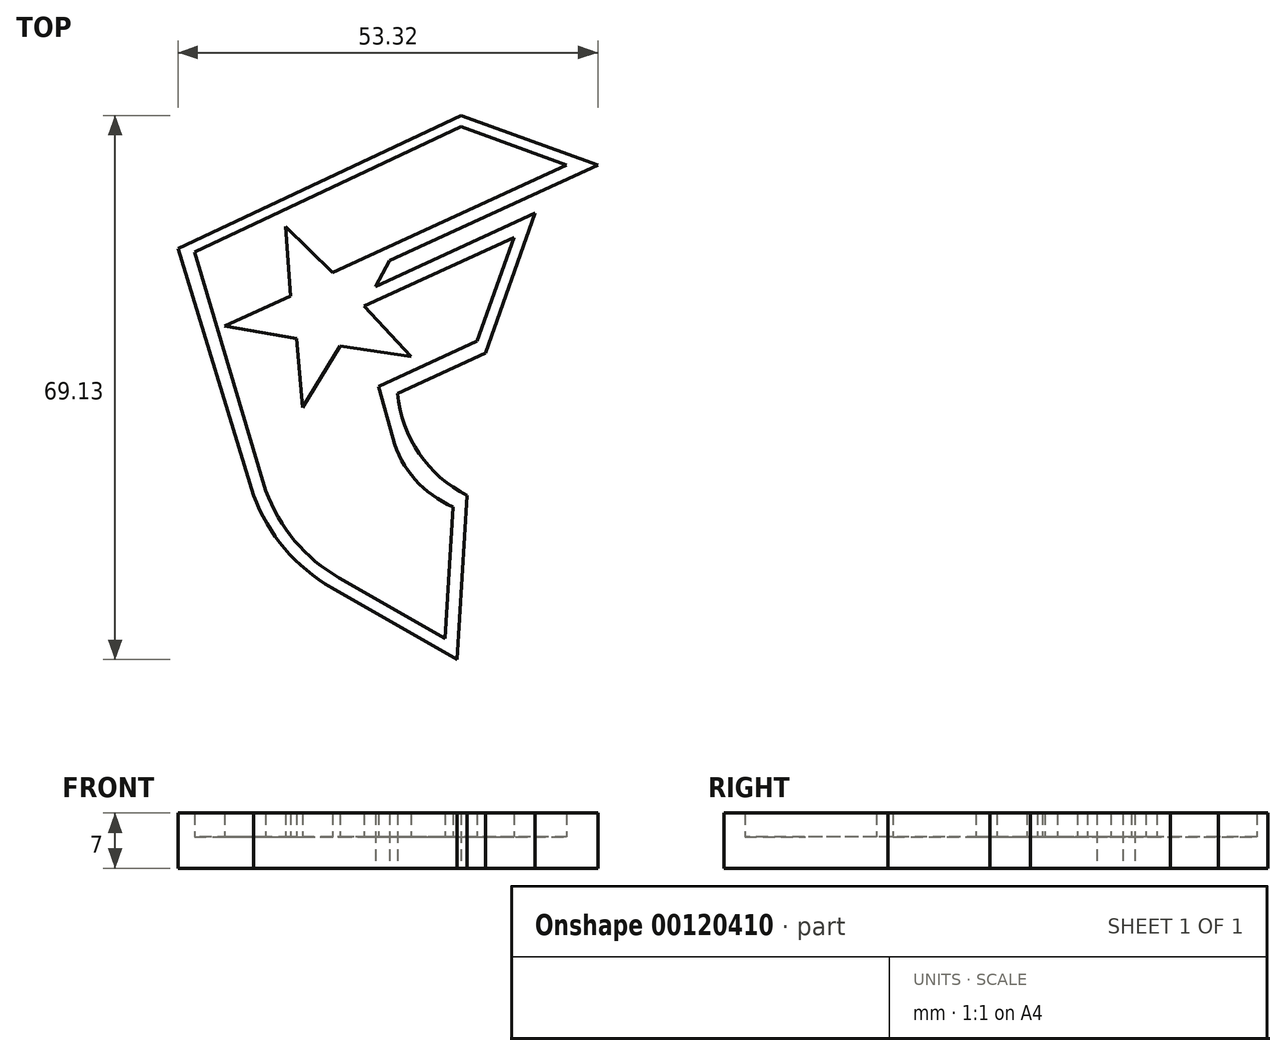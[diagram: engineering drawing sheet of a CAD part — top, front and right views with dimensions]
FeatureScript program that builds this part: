
annotation { "Feature Type Name" : "Feature", "Feature Type Description" : "" }
export const myFeature = defineFeature(function(context is Context, id is Id, definition is map)
    precondition{}
    {
        {
            var Q0;
            Q0=qCreatedBy(makeId("Top.planeOp"),FACE);
            var sketch = newSketch(context, id + "F0", { "sketchPlane" : qUnion([Q0])});
            skLineSegment(sketch, "E0", {"start": v(-33.1, 17.08) * mm, "end": v(2.86, 33.98) * mm});
            skLineSegment(sketch, "E1", {"start": v(2.86, 33.98) * mm, "end": v(20.22, 27.65) * mm});
            skLineSegment(sketch, "E2", {"start": v(20.22, 27.65) * mm, "end": v(-6.25, 15.54) * mm});
            skLineSegment(sketch, "E3", {"start": v(-6.25, 15.54) * mm, "end": v(-8.03, 12.25) * mm});
            skLineSegment(sketch, "E4", {"start": v(-8.03, 12.25) * mm, "end": v(12.24, 21.55) * mm});
            skLineSegment(sketch, "E5", {"start": v(12.24, 21.55) * mm, "end": v(5.96, 3.8) * mm});
            skLineSegment(sketch, "E6", {"start": v(5.96, 3.8) * mm, "end": v(-5.21, -1.36) * mm});
            skArc(sketch, "E7", {"start": v(-5.21, -1.36) * mm, "mid": v(-2.48, -8.98) * mm, "end": v(3.6, -14.3) * mm});
            skLineSegment(sketch, "E8", {"start": v(3.6, -14.3) * mm, "end": v(2.3, -35.15) * mm});
            skLineSegment(sketch, "E9", {"start": v(2.3, -35.15) * mm, "end": v(-13.57, -26.04) * mm});
            skArc(sketch, "E10", {"start": v(-23.52, -14.3) * mm, "mid": v(-19.57, -21.05) * mm, "end": v(-13.57, -26.04) * mm});
            skLineSegment(sketch, "E11", {"start": v(-23.52, -14.3) * mm, "end": v(-33.1, 17.08) * mm});
            skLineSegment(sketch, "E12", {"start": v(-31.03, 16.6) * mm, "end": v(2.86, 32.53) * mm});
            skLineSegment(sketch, "E13", {"start": v(2.86, 32.53) * mm, "end": v(16.25, 27.65) * mm});
            skLineSegment(sketch, "E14", {"start": v(16.25, 27.65) * mm, "end": v(-13.5, 14.04) * mm});
            skLineSegment(sketch, "E15", {"start": v(-13.5, 14.04) * mm, "end": v(-19.48, 19.86) * mm});
            skLineSegment(sketch, "E16", {"start": v(-19.48, 19.86) * mm, "end": v(-18.85, 11.02) * mm});
            skLineSegment(sketch, "E17", {"start": v(-18.85, 11.02) * mm, "end": v(-27.22, 7.23) * mm});
            skLineSegment(sketch, "E18", {"start": v(-27.22, 7.23) * mm, "end": v(-18.06, 5.6) * mm});
            skLineSegment(sketch, "E19", {"start": v(-18.06, 5.6) * mm, "end": v(-17.31, -3.11) * mm});
            skLineSegment(sketch, "E20", {"start": v(-17.31, -3.11) * mm, "end": v(-12.53, 4.66) * mm});
            skLineSegment(sketch, "E21", {"start": v(-12.53, 4.66) * mm, "end": v(-3.54, 3.32) * mm});
            skLineSegment(sketch, "E22", {"start": v(-3.54, 3.32) * mm, "end": v(-9.5, 9.75) * mm});
            skLineSegment(sketch, "E23", {"start": v(-9.5, 9.75) * mm, "end": v(9.56, 18.49) * mm});
            skLineSegment(sketch, "E24", {"start": v(9.56, 18.49) * mm, "end": v(4.9, 5.32) * mm});
            skLineSegment(sketch, "E25", {"start": v(4.9, 5.32) * mm, "end": v(-7.65, -0.47) * mm});
            skLineSegment(sketch, "E26", {"start": v(-7.65, -0.47) * mm, "end": v(-5.83, -7.06) * mm});
            skArc(sketch, "E27", {"start": v(-5.83, -7.06) * mm, "mid": v(-3, -12.28) * mm, "end": v(1.83, -15.74) * mm});
            skLineSegment(sketch, "E28", {"start": v(1.83, -15.74) * mm, "end": v(0.77, -32.48) * mm});
            skLineSegment(sketch, "E29", {"start": v(0.77, -32.48) * mm, "end": v(-12.64, -24.79) * mm});
            skArc(sketch, "E30", {"start": v(-21.97, -13.69) * mm, "mid": v(-18.28, -20.06) * mm, "end": v(-12.64, -24.79) * mm});
            skLineSegment(sketch, "E31", {"start": v(-21.97, -13.69) * mm, "end": v(-31.03, 16.6) * mm});
            skLineSegment(sketch, "E32", {"start": v(-15.12, 25.53) * mm, "end": v(-10.6, 27.66) * mm});
            skLineSegment(sketch, "E33", {"start": v(-10.6, 27.66) * mm, "end": v(-12.72, 32.18) * mm});
            skArc(sketch, "E34", {"start": v(-12.72, 32.18) * mm, "mid": v(-15.55, 34.76) * mm, "end": v(-19.38, 34.58) * mm});
            skArc(sketch, "E35", {"start": v(-16.19, 27.8) * mm, "mid": v(-14.99, 31.12) * mm, "end": v(-18.31, 32.32) * mm});
            skLineSegment(sketch, "E36.MirrorCS", {"start": v(-19.65, 23.4) * mm, "end": v(-21.77, 27.93) * mm});
            skArc(sketch, "E37.MirrorCS", {"start": v(-21.77, 27.93) * mm, "mid": v(-21.95, 31.75) * mm, "end": v(-19.38, 34.58) * mm});
            skArc(sketch, "E38.MirrorCS", {"start": v(-16.19, 27.8) * mm, "mid": v(-19.51, 29) * mm, "end": v(-18.31, 32.32) * mm});
            skLineSegment(sketch, "E39.MirrorCS", {"start": v(-15.12, 25.53) * mm, "end": v(-19.65, 23.4) * mm});
            skSolve(sketch);
        }
        {
            var Q0;
            {var subQ1=sQuery(id+"F0.wireOp",EDGE,"E1");Q0=makeQuery(id+"F0.imprint","IMPRINT",FACE,{"disambiguationData":[TD([[makeQuery(id+"F0.imprint","IMPRINT",EDGE,{"derivedFrom":subQ1}),-1.0]])]});}
            var Q1;
            Q1=makeQuery(id+"F0.imprint","IMPRINT",FACE,{"disambiguationData":[TD([[makeQuery(id+"F0.imprint","IMPRINT",EDGE,{"derivedFrom":sQuery(id+"F0.wireOp",EDGE,"E32")}),1.0]])]});
            var Q2;
            {var subQ0=sQuery(id+"F0.wireOp",EDGE,"KOQnUoiF-NE6V-rC7K-aeo2-cwmYvovwqncn");Q2=makeQuery(id+"F0.imprint","IMPRINT",FACE,{"disambiguationData":[TD([[makeQuery(id+"F0.imprint","IMPRINT",EDGE,{"derivedFrom":subQ0}),-1.0]])]});}
            extrude(context, id + "F1", {"entities" : qUnion([Q0, Q1, Q2]), "depth" : 7 * mm});
        }
        {
            var Q0;
            Q0=makeQuery(id+"F1.opExtrude","CAP_FACE",FACE,{"disambiguationData":[OSD([sQuery(id+"F0.wireOp",EDGE,"E0"),sQuery(id+"F0.wireOp",EDGE,"E1"),sQuery(id+"F0.wireOp",EDGE,"E2"),sQuery(id+"F0.wireOp",EDGE,"E3"),sQuery(id+"F0.wireOp",EDGE,"E4"),sQuery(id+"F0.wireOp",EDGE,"E5"),sQuery(id+"F0.wireOp",EDGE,"E6"),sQuery(id+"F0.wireOp",EDGE,"E7"),sQuery(id+"F0.wireOp",EDGE,"E8"),sQuery(id+"F0.wireOp",EDGE,"E9"),sQuery(id+"F0.wireOp",EDGE,"E10"),sQuery(id+"F0.wireOp",EDGE,"E11"),sQuery(id+"F0.wireOp",EDGE,"E12"),sQuery(id+"F0.wireOp",EDGE,"E13"),sQuery(id+"F0.wireOp",EDGE,"E14"),sQuery(id+"F0.wireOp",EDGE,"E15"),sQuery(id+"F0.wireOp",EDGE,"E16"),sQuery(id+"F0.wireOp",EDGE,"E17"),sQuery(id+"F0.wireOp",EDGE,"E18"),sQuery(id+"F0.wireOp",EDGE,"E19"),sQuery(id+"F0.wireOp",EDGE,"E20"),sQuery(id+"F0.wireOp",EDGE,"E21"),sQuery(id+"F0.wireOp",EDGE,"E22"),sQuery(id+"F0.wireOp",EDGE,"E23"),sQuery(id+"F0.wireOp",EDGE,"E24"),sQuery(id+"F0.wireOp",EDGE,"E25"),sQuery(id+"F0.wireOp",EDGE,"E26"),sQuery(id+"F0.wireOp",EDGE,"E27"),sQuery(id+"F0.wireOp",EDGE,"E28"),sQuery(id+"F0.wireOp",EDGE,"E29"),sQuery(id+"F0.wireOp",EDGE,"E30"),sQuery(id+"F0.wireOp",EDGE,"E31"),sQuery(id+"F0.wireOp",EDGE,"LDBnH7SO-8LKQ-1sHw-Y3xK-lkZMPvaqYCBa"),sQuery(id+"F0.wireOp",EDGE,"4d6fbee4-d8c1-4914-8c66-ae823deec88e0.MirrorCS"),sQuery(id+"F0.wireOp",EDGE,"Br9sVRIy-d93E-y2kv-yzfS-C45cdY2g4OVA"),sQuery(id+"F0.wireOp",EDGE,"cr9mcGUi-bcfW-oMh8-YYdQ-1kwbzuUjQ3jj")])],"isStart":true});
            var sketch = newSketch(context, id + "F2", { "sketchPlane" : qUnion([Q0])});
            skLineSegment(sketch, "E40", {"start": v(-33.1, -17.08) * mm, "end": v(-23.52, 14.3) * mm});
            skArc(sketch, "E41", {"start": v(-13.57, 26.04) * mm, "mid": v(-19.57, 21.05) * mm, "end": v(-23.52, 14.3) * mm});
            skLineSegment(sketch, "E42", {"start": v(-13.57, 26.04) * mm, "end": v(2.3, 35.15) * mm});
            skLineSegment(sketch, "E43", {"start": v(2.3, 35.15) * mm, "end": v(3.6, 14.3) * mm});
            skArc(sketch, "E44", {"start": v(3.6, 14.3) * mm, "mid": v(-2.46, 8.97) * mm, "end": v(-5.21, 1.36) * mm});
            skLineSegment(sketch, "E45", {"start": v(-5.21, 1.36) * mm, "end": v(5.96, -3.8) * mm});
            skLineSegment(sketch, "E46", {"start": v(5.96, -3.8) * mm, "end": v(12.24, -21.55) * mm});
            skLineSegment(sketch, "E47", {"start": v(12.24, -21.55) * mm, "end": v(-8.03, -12.25) * mm});
            skLineSegment(sketch, "E48", {"start": v(-8.03, -12.25) * mm, "end": v(-6.25, -15.54) * mm});
            skLineSegment(sketch, "E49", {"start": v(-6.25, -15.54) * mm, "end": v(20.22, -27.65) * mm});
            skLineSegment(sketch, "E50", {"start": v(20.22, -27.65) * mm, "end": v(2.86, -33.98) * mm});
            skLineSegment(sketch, "E51", {"start": v(2.86, -33.98) * mm, "end": v(-33.1, -17.08) * mm});
            skSolve(sketch);
        }
        {
            var Q0;
            Q0=makeQuery(id+"F2.imprint","IMPRINT",FACE,{"disambiguationData":[TD([[makeQuery(id+"F2.imprint","IMPRINT",EDGE,{"derivedFrom":makeQuery(id+"F1.opExtrude","CAP_EDGE",EDGE,{"disambiguationData":[OSD([sQuery(id+"F0.wireOp",EDGE,"E12")])],"isStart":true})}),1.0]])]});
            extrude(context, id + "F3", {"entities" : qUnion([Q0]), "operationType" : NewBodyOperationType.ADD, "oppositeDirection" : true, "depth" : 4 * mm});
        }
    });
